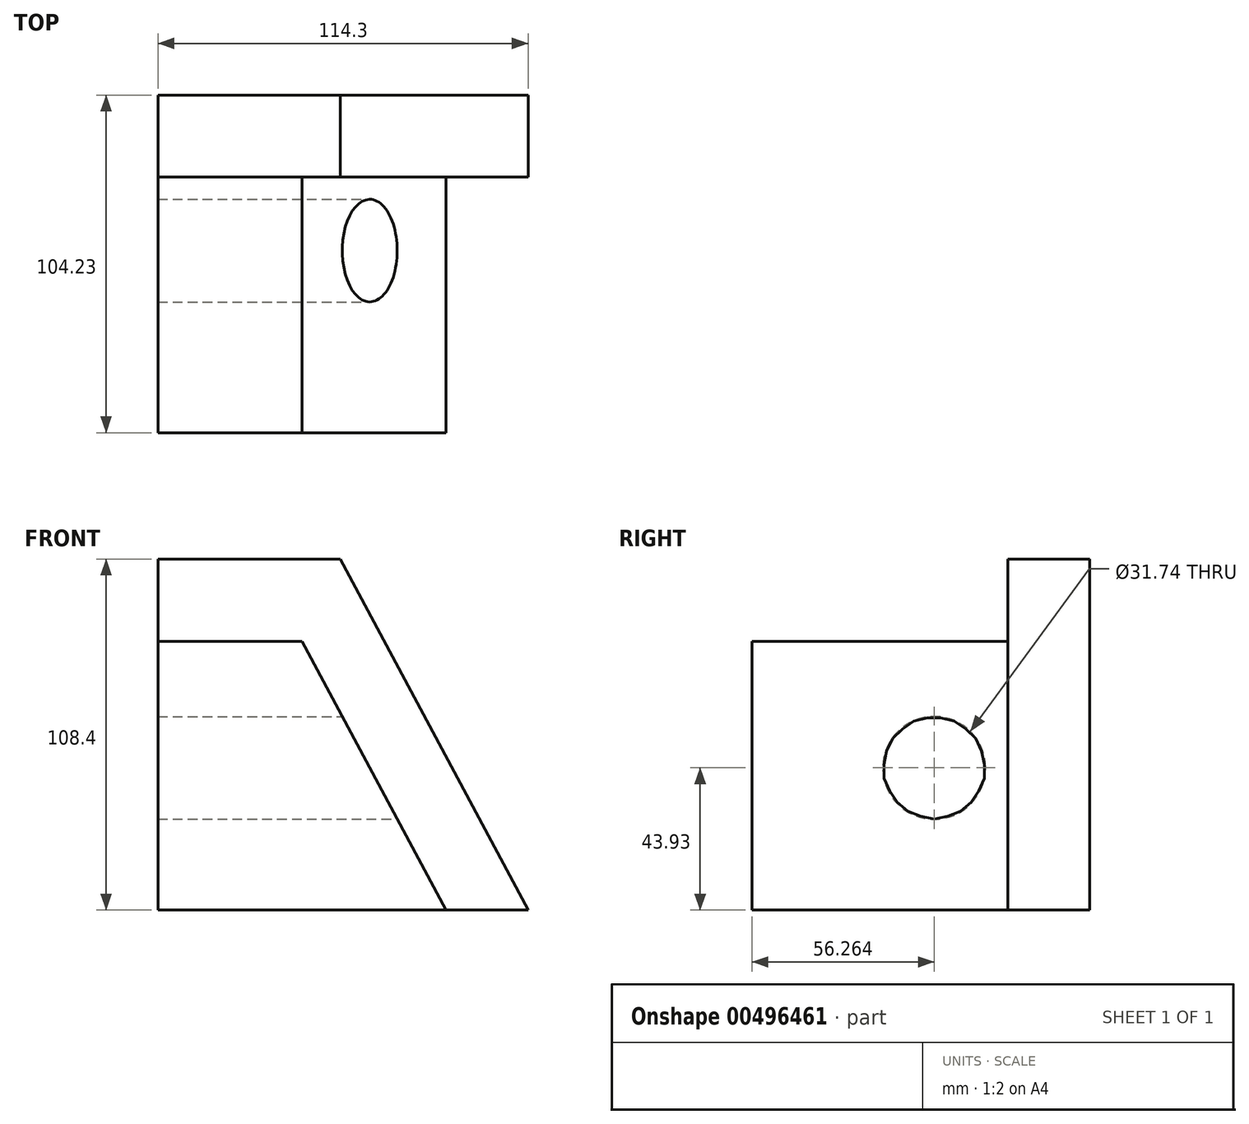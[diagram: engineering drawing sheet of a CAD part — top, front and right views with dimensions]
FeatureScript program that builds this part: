
annotation { "Feature Type Name" : "Feature", "Feature Type Description" : "" }
export const myFeature = defineFeature(function(context is Context, id is Id, definition is map)
    precondition{}
    {
        {
            var Q0;
            Q0=qCreatedBy(makeId("Right.planeOp"),FACE);
            var sketch = newSketch(context, id + "F0", { "sketchPlane" : qUnion([Q0])});
            skLineSegment(sketch, "E0.bottom", {"start": v(-38.74, 39.07) * mm, "end": v(65.49, 39.07) * mm});
            skLineSegment(sketch, "E0.top", {"start": v(-38.74, -43.93) * mm, "end": v(65.49, -43.93) * mm});
            skLineSegment(sketch, "E0.left", {"start": v(-38.74, 39.07) * mm, "end": v(-38.74, -43.93) * mm});
            skLineSegment(sketch, "E0.right", {"start": v(65.49, 39.07) * mm, "end": v(65.49, -43.93) * mm});
            skCircle(sketch, "E1", {"center": v(17.52, 0) * mm, "radius": 15.87 * mm});
            skSolve(sketch);
        }
        {
            var Q0;
            Q0=makeQuery(id+"F0.imprint","IMPRINT",FACE,{"disambiguationData":[TD([[makeQuery(id+"F0.imprint","IMPRINT",EDGE,{"derivedFrom":sQuery(id+"F0.wireOp",EDGE,"E0.bottom")}),-1.0]])]});
            extrude(context, id + "F1", {"entities" : qUnion([Q0]), "oppositeDirection" : true, "depth" : 88.9 * mm});
        }
        {
            var Q0;
            Q0=makeQuery(id+"F1.opExtrude","SWEPT_FACE",FACE,{"disambiguationData":[OSD([sQuery(id+"F0.wireOp",EDGE,"E0.left")])]});
            var sketch = newSketch(context, id + "F2", { "sketchPlane" : qUnion([Q0])});
            skLineSegment(sketch, "E2", {"start": v(-44.45, 39.07) * mm, "end": v(0, -43.93) * mm});
            skLineSegment(sketch, "E3", {"start": v(0, -43.93) * mm, "end": v(0, 39.07) * mm});
            skLineSegment(sketch, "E4", {"start": v(0, 39.07) * mm, "end": v(-44.45, 39.07) * mm});
            skSolve(sketch);
        }
        {
            var Q0;
            Q0=makeQuery(id+"F2.imprint","IMPRINT",FACE,{"disambiguationData":[TD([[makeQuery(id+"F2.imprint","IMPRINT",EDGE,{"derivedFrom":sQuery(id+"F2.wireOp",EDGE,"E2")}),1.0]])]});
            extrude(context, id + "F3", {"entities" : qUnion([Q0]), "operationType" : NewBodyOperationType.REMOVE, "oppositeDirection" : true, "depth" : 152.4 * mm});
        }
        {
            var Q0;
            Q0=makeQuery(id+"F1.opExtrude","SWEPT_FACE",FACE,{"disambiguationData":[OSD([sQuery(id+"F0.wireOp",EDGE,"E0.bottom")])]});
            var sketch = newSketch(context, id + "F4", { "sketchPlane" : qUnion([Q0])});
            skLineSegment(sketch, "E5.bottom", {"start": v(-88.9, 65.49) * mm, "end": v(-44.45, 65.49) * mm});
            skLineSegment(sketch, "E5.top", {"start": v(-88.9, 40.28) * mm, "end": v(-44.45, 40.28) * mm});
            skLineSegment(sketch, "E5.left", {"start": v(-88.9, 65.49) * mm, "end": v(-88.9, 40.28) * mm});
            skLineSegment(sketch, "E5.right", {"start": v(-44.45, 65.49) * mm, "end": v(-44.45, 40.28) * mm});
            skSolve(sketch);
        }
        {
            var Q0;
            Q0=makeQuery(id+"F4.imprint","IMPRINT",FACE,{"disambiguationData":[TD([[makeQuery(id+"F4.imprint","IMPRINT",EDGE,{"derivedFrom":sQuery(id+"F4.wireOp",EDGE,"E5.bottom")}),-1.0]])]});
            extrude(context, id + "F5", {"entities" : qUnion([Q0]), "operationType" : NewBodyOperationType.ADD, "depth" : 25.4 * mm});
        }
        {
            var Q0;
            Q0=makeQuery(id+"F3.boolean.opBoolean","COPY",FACE,{"derivedFrom":makeQuery(id+"F3.opExtrude","SWEPT_FACE",FACE,{"disambiguationData":[OSD([sQuery(id+"F2.wireOp",EDGE,"E2")])]})});
            var sketch = newSketch(context, id + "F6", { "sketchPlane" : qUnion([Q0])});
            skLineSegment(sketch, "E6", {"start": v(40.28, 55.43) * mm, "end": v(40.28, -38.72) * mm});
            skSolve(sketch);
        }
        {
            var Q0;
            Q0=makeQuery(id+"F5.opExtrude","SWEPT_FACE",FACE,{"disambiguationData":[OSD([sQuery(id+"F4.wireOp",EDGE,"E5.right")])]});
            var Q1;
            {var subQ0=sQuery(id+"F6.wireOp",EDGE,"E6");Q1=makeQuery(id+"F6.imprint","IMPRINT",FACE,{"disambiguationData":[TD([[makeQuery(id+"F6.imprint","IMPRINT",EDGE,{"derivedFrom":subQ0}),1.0]])]});}
            extrude(context, id + "F7", {"entities" : qUnion([Q0, Q1]), "operationType" : NewBodyOperationType.ADD, "depth" : 25.4 * mm, "hasSecondDirection" : true, "secondDirectionOppositeDirection" : true, "secondDirectionDepth" : 25.4 * mm});
        }
        {
            var Q0;
            {var subQ0=sQuery(id+"F4.wireOp",EDGE,"E5.top");Q0=makeQuery(id+"F7.boolean.opBoolean","MERGE",FACE,{"derivedFrom":[makeQuery(id+"F5.opExtrude","SWEPT_FACE",FACE,{"disambiguationData":[OSD([subQ0])]}),makeQuery(id+"F7.opExtrude","SWEPT_FACE",FACE,{"disambiguationData":[OSD([sQuery(id+"F0.wireOp",EDGE,"E0.bottom"),sQuery(id+"F0.wireOp",EDGE,"E0.left"),sQuery(id+"F2.wireOp",EDGE,"E2"),sQuery(id+"F2.wireOp",EDGE,"E4"),subQ0,sQuery(id+"F4.wireOp",EDGE,"E5.right")])]}),makeQuery(id+"F7.opExtrude","SWEPT_FACE",FACE,{"disambiguationData":[OSD([sQuery(id+"F6.wireOp",EDGE,"E6")])]})]});}
            var sketch = newSketch(context, id + "F8", { "sketchPlane" : qUnion([Q0])});
            skLineSegment(sketch, "E7", {"start": v(-19.05, 39.07) * mm, "end": v(-32.65, 64.47) * mm});
            skLineSegment(sketch, "E8", {"start": v(-32.65, 64.47) * mm, "end": v(-19.05, 64.47) * mm});
            skLineSegment(sketch, "E9", {"start": v(-19.05, 64.47) * mm, "end": v(-19.05, 39.07) * mm});
            skSolve(sketch);
        }
        {
            var Q0;
            Q0=makeQuery(id+"F8.imprint","IMPRINT",FACE,{"disambiguationData":[TD([[makeQuery(id+"F8.imprint","IMPRINT",EDGE,{"derivedFrom":sQuery(id+"F8.wireOp",EDGE,"E7")}),-1.0]])]});
            extrude(context, id + "F9", {"entities" : qUnion([Q0]), "operationType" : NewBodyOperationType.REMOVE, "endBound" : BoundingType.THROUGH_ALL, "oppositeDirection" : true, "depth" : 25.4 * mm});
        }
    });
